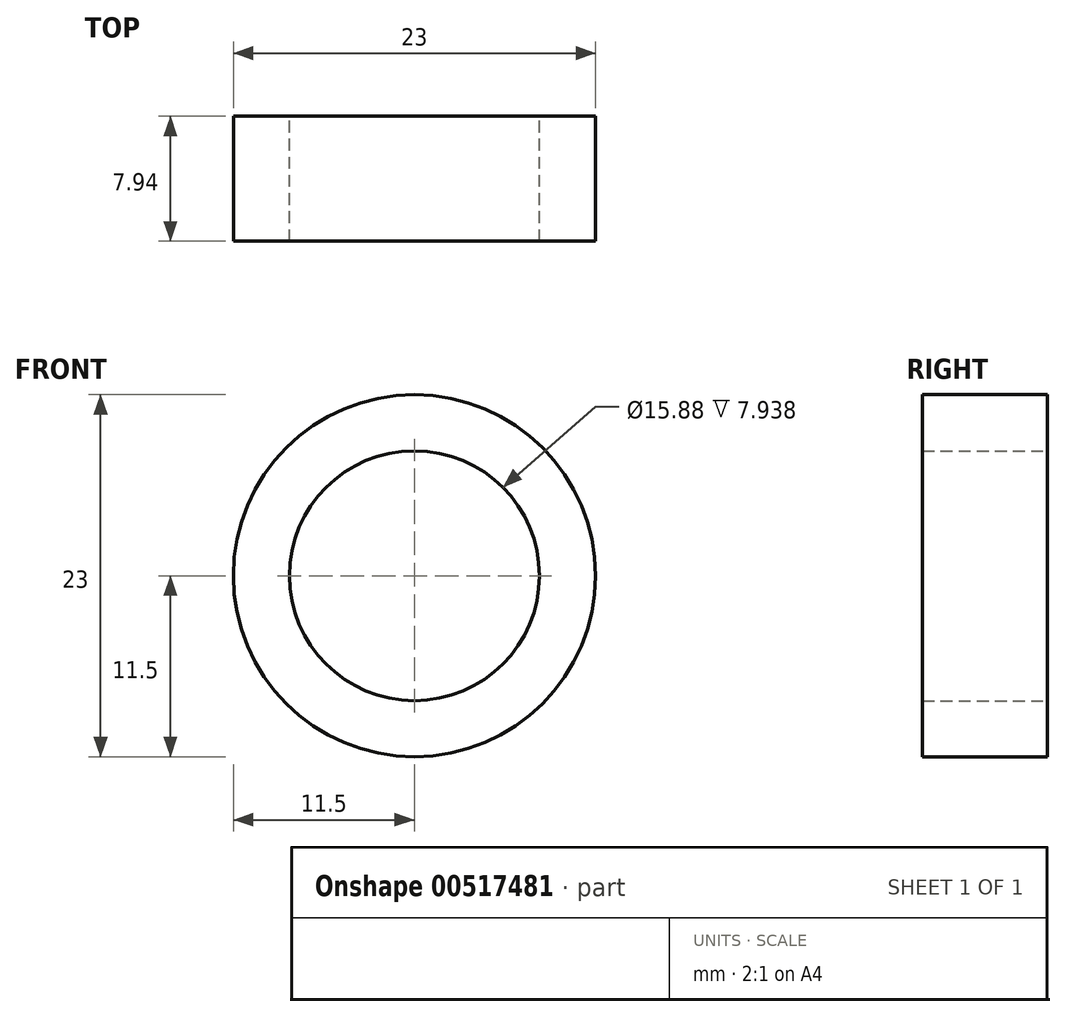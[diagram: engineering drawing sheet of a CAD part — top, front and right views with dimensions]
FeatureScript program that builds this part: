
annotation { "Feature Type Name" : "Feature", "Feature Type Description" : "" }
export const myFeature = defineFeature(function(context is Context, id is Id, definition is map)
    precondition{}
    {
        {
            var Q0;
            Q0=qCreatedBy(makeId("Front.planeOp"),FACE);
            var sketch = newSketch(context, id + "F0", { "sketchPlane" : qUnion([Q0])});
            skCircle(sketch, "E0", {"center": v(0, 0) * mm, "radius": 11.5 * mm});
            skCircle(sketch, "E1", {"center": v(0, 0) * mm, "radius": 7.94 * mm});
            skSolve(sketch);
        }
        {
            var Q0;
            Q0 = qSketchRegion(id + "F0", true);
            extrude(context, id + "F1", {"entities" : qUnion([Q0]), "depth" : 7.94 * mm, "offsetDistance" : 25.4 * mm});
        }
    });
